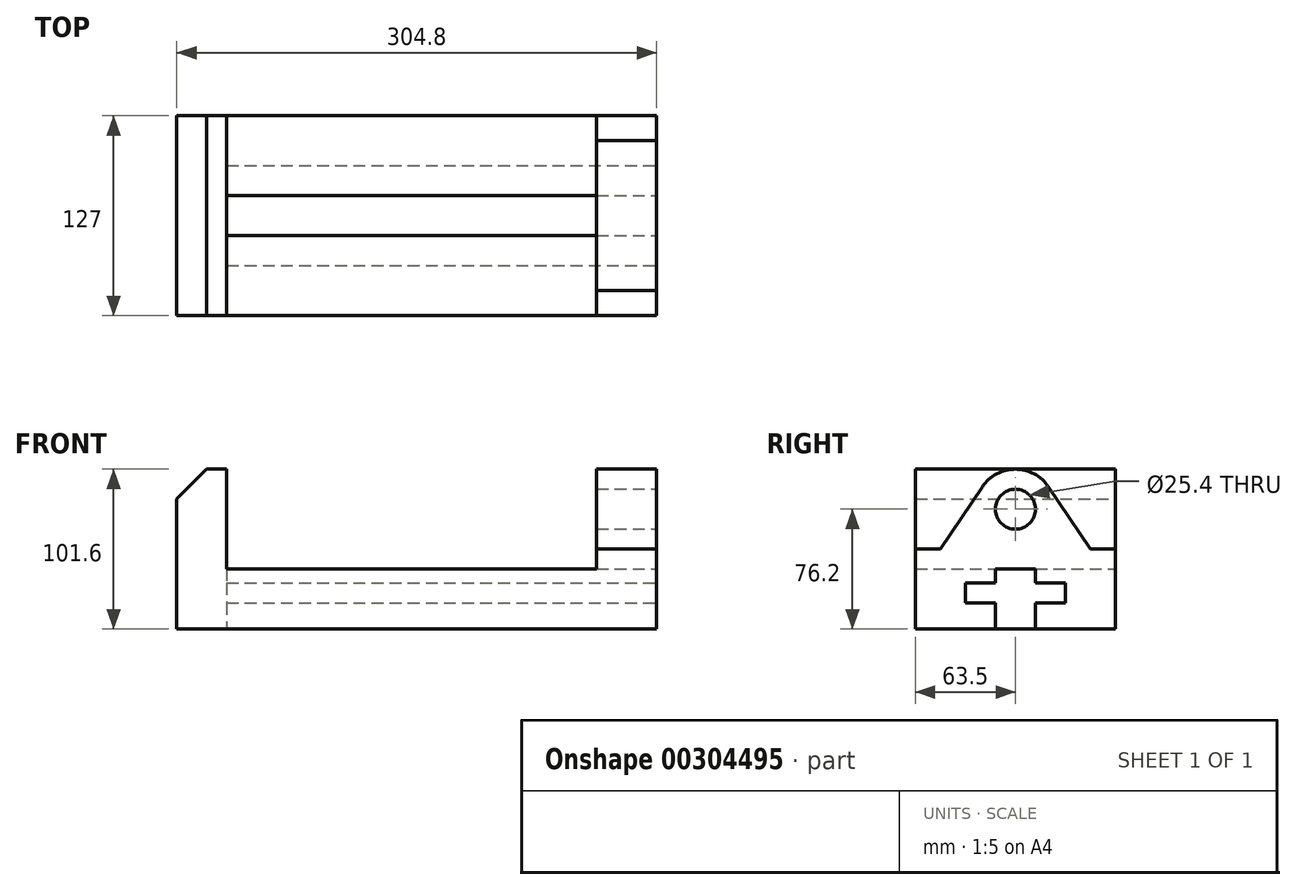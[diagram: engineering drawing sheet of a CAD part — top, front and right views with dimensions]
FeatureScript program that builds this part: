
annotation { "Feature Type Name" : "Feature", "Feature Type Description" : "" }
export const myFeature = defineFeature(function(context is Context, id is Id, definition is map)
    precondition{}
    {
        {
            var Q0;
            Q0=qCreatedBy(makeId("Front.planeOp"),FACE);
            var sketch = newSketch(context, id + "F0", { "sketchPlane" : qUnion([Q0])});
            skLineSegment(sketch, "E0.bottom", {"start": v(0, 0) * mm, "end": v(304.8, 0) * mm});
            skLineSegment(sketch, "E0.top", {"start": v(31.75, 38.1) * mm, "end": v(266.7, 38.1) * mm});
            skLineSegment(sketch, "E0.left", {"start": v(0, 0) * mm, "end": v(0, 38.1) * mm});
            skLineSegment(sketch, "E0.right", {"start": v(304.8, 0) * mm, "end": v(304.8, 38.1) * mm});
            skLineSegment(sketch, "E1.top", {"start": v(304.8, 50.8) * mm, "end": v(266.7, 50.8) * mm});
            skLineSegment(sketch, "E1.left", {"start": v(304.8, 38.1) * mm, "end": v(304.8, 50.8) * mm});
            skLineSegment(sketch, "E1.right", {"start": v(266.7, 38.1) * mm, "end": v(266.7, 50.8) * mm});
            skLineSegment(sketch, "E2.top", {"start": v(0, 101.6) * mm, "end": v(31.75, 101.6) * mm});
            skLineSegment(sketch, "E2.left", {"start": v(0, 38.1) * mm, "end": v(0, 101.6) * mm});
            skLineSegment(sketch, "E2.right", {"start": v(31.75, 38.1) * mm, "end": v(31.75, 101.6) * mm});
            skSolve(sketch);
        }
        {
            var Q0;
            Q0 = qSketchRegion(id + "F0", true);
            extrude(context, id + "F1", {"entities" : qUnion([Q0]), "endBound" : BoundingType.SYMMETRIC, "depth" : 127 * mm});
        }
        {
            var Q0;
            Q0=makeQuery(id+"F1.opExtrude","SWEPT_EDGE",EDGE,{"disambiguationData":[OSD([sQuery(id+"F0.wireOp",EDGE,"E2.top"),sQuery(id+"F0.wireOp",EDGE,"E2.left")])]});
            chamfer(context, id + "F2", {"entities" : qUnion([Q0]), "chamferType" : ChamferType.TWO_OFFSETS, "width1" : 19.05 * mm, "oppositeDirection" : false, "width2" : 19.05 * mm, "tangentPropagation" : true});
        }
        {
            var Q0;
            Q0=makeQuery(id+"F1.opExtrude","SWEPT_FACE",FACE,{"disambiguationData":[OSD([sQuery(id+"F0.wireOp",EDGE,"E0.right"),sQuery(id+"F0.wireOp",EDGE,"E1.left")])]});
            var sketch = newSketch(context, id + "F3", { "sketchPlane" : qUnion([Q0])});
            skLineSegment(sketch, "E3", {"start": v(-12.7, 0) * mm, "end": v(12.7, 0) * mm});
            skLineSegment(sketch, "E4", {"start": v(12.7, 0) * mm, "end": v(12.7, 16.51) * mm});
            skLineSegment(sketch, "E5", {"start": v(12.7, 16.51) * mm, "end": v(31.75, 16.51) * mm});
            skLineSegment(sketch, "E6", {"start": v(31.75, 16.51) * mm, "end": v(31.75, 29.2) * mm});
            skLineSegment(sketch, "E7", {"start": v(31.75, 29.21) * mm, "end": v(12.7, 29.21) * mm});
            skLineSegment(sketch, "E8", {"start": v(12.7, 29.21) * mm, "end": v(12.7, 38.1) * mm});
            skLineSegment(sketch, "E9", {"start": v(12.7, 38.1) * mm, "end": v(-12.7, 38.1) * mm});
            skLineSegment(sketch, "E10", {"start": v(-12.7, 38.1) * mm, "end": v(-12.7, 29.21) * mm});
            skLineSegment(sketch, "E11", {"start": v(-12.7, 29.21) * mm, "end": v(-31.75, 29.2) * mm});
            skLineSegment(sketch, "E12", {"start": v(-31.75, 29.2) * mm, "end": v(-31.75, 16.51) * mm});
            skLineSegment(sketch, "E13", {"start": v(-31.75, 16.51) * mm, "end": v(-12.7, 16.51) * mm});
            skLineSegment(sketch, "E14", {"start": v(-12.7, 16.51) * mm, "end": v(-12.7, 0) * mm});
            skSolve(sketch);
        }
        {
            var Q0;
            Q0 = qSketchRegion(id + "F3", true);
            var Q1;
            Q1=makeQuery(id+"F1.opExtrude","SWEPT_FACE",FACE,{"disambiguationData":[OSD([sQuery(id+"F0.wireOp",EDGE,"E2.right")])]});
            extrude(context, id + "F4", {"entities" : qUnion([Q0]), "operationType" : NewBodyOperationType.REMOVE, "endBound" : BoundingType.UP_TO_SURFACE, "oppositeDirection" : true, "endBoundEntityFace" : qUnion([Q1]), "depth" : 25.4 * mm});
        }
        {
            var Q0;
            Q0=makeQuery(id+"F1.opExtrude","SWEPT_FACE",FACE,{"disambiguationData":[OSD([sQuery(id+"F0.wireOp",EDGE,"E0.right"),sQuery(id+"F0.wireOp",EDGE,"E1.left")])]});
            var sketch = newSketch(context, id + "F5", { "sketchPlane" : qUnion([Q0])});
            skLineSegment(sketch, "E15", {"start": v(-47.63, 50.8) * mm, "end": v(-21.1, 90.35) * mm});
            skLineSegment(sketch, "E16", {"start": v(21.1, 90.35) * mm, "end": v(47.63, 50.8) * mm});
            skLineSegment(sketch, "E17", {"start": v(47.63, 50.8) * mm, "end": v(-47.63, 50.8) * mm});
            skPoint(sketch, "E18.visualSharp", {"position": v(0, 121.8) * mm});
            skArc(sketch, "E18.filletArc", {"start": v(21.1, 90.35) * mm, "mid": v(0, 101.6) * mm, "end": v(-21.1, 90.35) * mm});
            skPoint(sketch, "E19", {"position": v(0, 101.6) * mm});
            skLineSegment(sketch, "E20", {"start": v(-63.5, 50.8) * mm, "end": v(-47.63, 50.8) * mm});
            skLineSegment(sketch, "E21", {"start": v(63.5, 50.8) * mm, "end": v(-63.5, 50.8) * mm});
            skPoint(sketch, "E22", {"position": v(0, 50.8) * mm});
            skLineSegment(sketch, "E23", {"start": v(-47.63, 50.8) * mm, "end": v(47.63, 50.8) * mm, "construction": true});
            skCircle(sketch, "E24", {"center": v(0, 76.2) * mm, "radius": 12.7 * mm});
            skSolve(sketch);
        }
        {
            var Q0;
            Q0 = qSketchRegion(id + "F5", true);
            var Q1;
            Q1=makeQuery(id+"F1.opExtrude","SWEPT_FACE",FACE,{"disambiguationData":[OSD([sQuery(id+"F0.wireOp",EDGE,"E1.right")])]});
            extrude(context, id + "F6", {"entities" : qUnion([Q0]), "operationType" : NewBodyOperationType.ADD, "endBound" : BoundingType.UP_TO_SURFACE, "oppositeDirection" : true, "endBoundEntityFace" : qUnion([Q1]), "depth" : 25.4 * mm});
        }
    });
